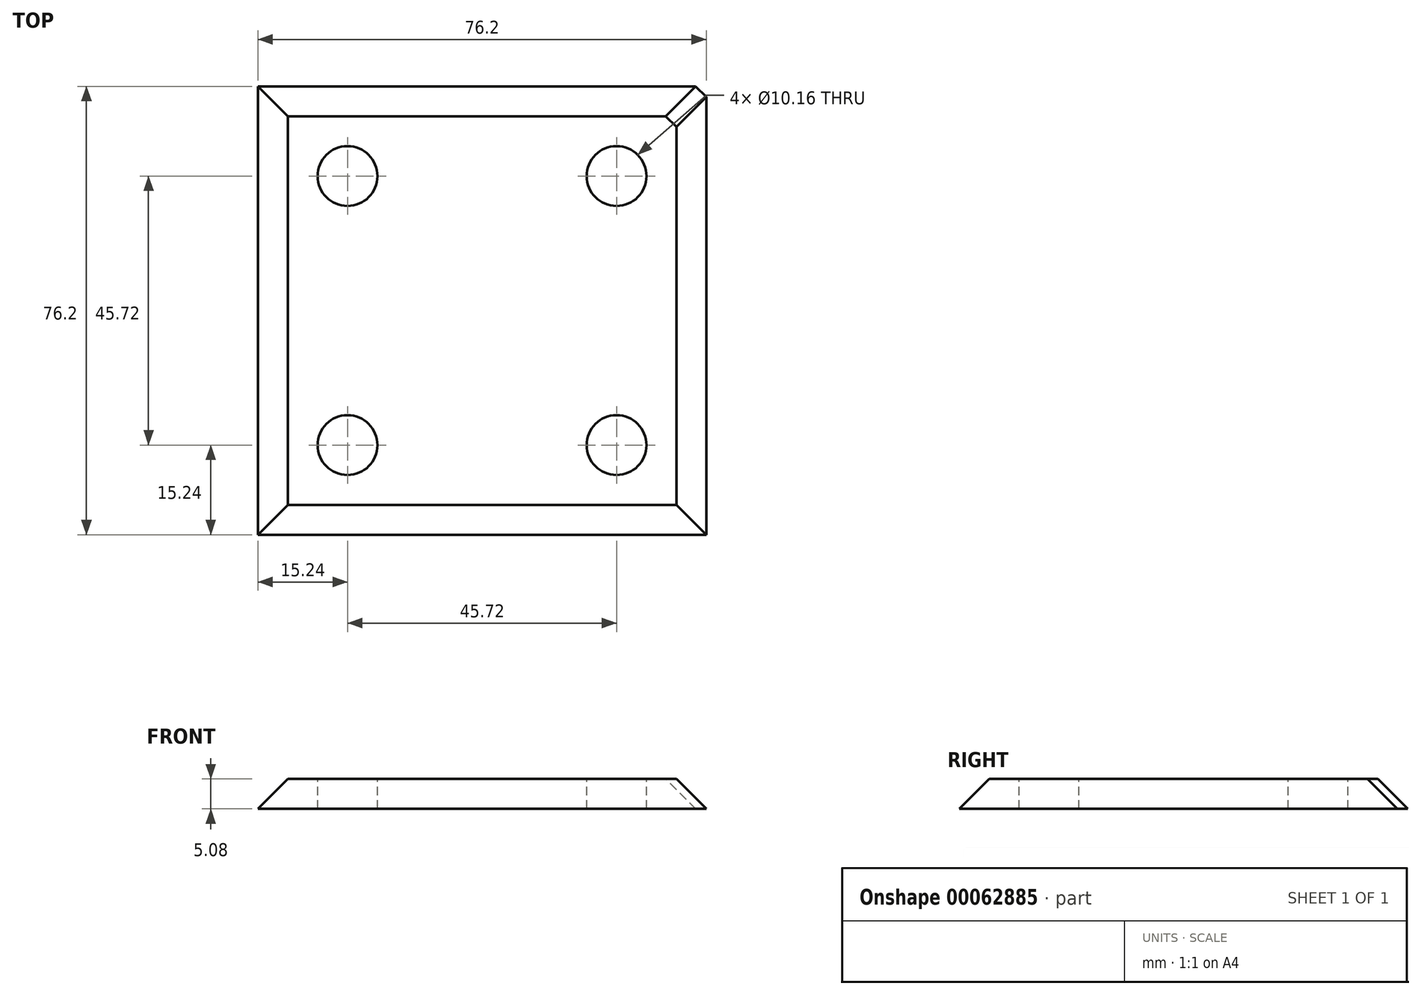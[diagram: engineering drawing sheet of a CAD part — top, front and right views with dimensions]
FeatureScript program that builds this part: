
annotation { "Feature Type Name" : "Feature", "Feature Type Description" : "" }
export const myFeature = defineFeature(function(context is Context, id is Id, definition is map)
    precondition{}
    {
        {
            var Q0;
            Q0=qCreatedBy(makeId("Top.planeOp"),FACE);
            var sketch = newSketch(context, id + "F0", { "sketchPlane" : qUnion([Q0])});
            skLineSegment(sketch, "E0.bottom", {"start": v(0, 0) * mm, "end": v(76.2, 0) * mm});
            skLineSegment(sketch, "E0.top", {"start": v(0, 76.2) * mm, "end": v(76.2, 76.2) * mm});
            skLineSegment(sketch, "E0.left", {"start": v(0, 0) * mm, "end": v(0, 76.2) * mm});
            skLineSegment(sketch, "E0.right", {"start": v(76.2, 0) * mm, "end": v(76.2, 76.2) * mm});
            skSolve(sketch);
        }
        {
            var Q0;
            Q0=qSketchRegion(id+"F0",true);
            extrude(context, id + "F1", {"entities" : qUnion([Q0]), "depth" : 5.08 * mm});
        }
        {
            var Q0;
            Q0=makeQuery(id+"F1.opExtrude","CAP_FACE",FACE,{"disambiguationData":[OSD([sQuery(id+"F0.wireOp",EDGE,"E0.bottom"),sQuery(id+"F0.wireOp",EDGE,"E0.top"),sQuery(id+"F0.wireOp",EDGE,"E0.left"),sQuery(id+"F0.wireOp",EDGE,"E0.right")])],"isStart":false});
            var sketch = newSketch(context, id + "F2", { "sketchPlane" : qUnion([Q0])});
            skCircle(sketch, "E1", {"center": v(15.24, 60.96) * mm, "radius": 5.08 * mm});
            skCircle(sketch, "E2", {"center": v(60.96, 60.96) * mm, "radius": 5.08 * mm});
            skCircle(sketch, "E3", {"center": v(15.24, 15.24) * mm, "radius": 5.08 * mm});
            skCircle(sketch, "E4", {"center": v(60.96, 15.24) * mm, "radius": 5.08 * mm});
            skSolve(sketch);
        }
        {
            var Q0;
            Q0=qSketchRegion(id+"F2",true);
            extrude(context, id + "F3", {"entities" : qUnion([Q0]), "operationType" : NewBodyOperationType.REMOVE, "oppositeDirection" : true, "depth" : 25.4 * mm});
        }
        {
            var Q0;
            Q0=makeQuery(id+"F1.opExtrude","CAP_EDGE",EDGE,{"disambiguationData":[OSD([sQuery(id+"F0.wireOp",EDGE,"E0.top")])],"isStart":false});
            var Q1;
            Q1=makeQuery(id+"F1.opExtrude","CAP_EDGE",EDGE,{"disambiguationData":[OSD([sQuery(id+"F0.wireOp",EDGE,"E0.left")])],"isStart":false});
            var Q2;
            Q2=makeQuery(id+"F1.opExtrude","CAP_EDGE",EDGE,{"disambiguationData":[OSD([sQuery(id+"F0.wireOp",EDGE,"E0.right")])],"isStart":false});
            var Q3;
            Q3=makeQuery(id+"F1.opExtrude","CAP_EDGE",EDGE,{"disambiguationData":[OSD([sQuery(id+"F0.wireOp",EDGE,"E0.bottom")])],"isStart":false});
            chamfer(context, id + "F4", {"entities" : qUnion([Q0, Q1, Q2, Q3]), "width" : 5.08 * mm, "tangentPropagation" : true});
        }
        {
            var Q0;
            Q0=makeQuery(id+"F4.opChamfer","BLEND_EDGE",EDGE,{"blendedFrom":[makeQuery(id+"F1.opExtrude","CAP_EDGE",EDGE,{"disambiguationData":[OSD([sQuery(id+"F0.wireOp",EDGE,"E0.top")])],"isStart":false}),makeQuery(id+"F1.opExtrude","CAP_EDGE",EDGE,{"disambiguationData":[OSD([sQuery(id+"F0.wireOp",EDGE,"E0.right")])],"isStart":false})],"blendedInto":[]});
            chamfer(context, id + "F5", {"entities" : qUnion([Q0]), "width" : 2.54 * mm, "tangentPropagation" : true});
        }
    });
